# Revit family: Shower-Valve_Trim-KOHLER-MODULO-K-99960T_1
name_source: partatom
category: Plumbing Fixtures
revit_build: Autodesk Revit 2017 (Build: 20160225_1515(x64)
units: mm (PartAtom-declared; Revit-internal decimal feet)

## family parameters
Cut with Voids When Loaded = No
Host = Face
OmniClass Number = 23.31.25.00
Part Type = Normal
Room Calculation Point = No
Round Connector Dimension = Use Diameter
Shared = No

## types (5) — shared parameters
ADA Compliant = No
Assembly Code = D2010700
CW Connection = Yes
Cold Water Inlet = Cold Water Inlet
Date Modified = 10/09/2020
Default Elevation = 42"
Description = Smart formula-shaped in-wall bathtub shower spool and panel—classic type (Mema handle)
Drain Included = No
Flow Rate = 0 GPM
HW Connection = Yes
Handle Clearance = 2 3/4"
Height = 7 1/16"
Hot Water Inlet = Hot Water Inlet
Length = 4 1/8"
Manufacturer = KOHLER Co.
Master Format 2014 = 22 42 23
Master Format 2014 Name = Residential Showers
Material = Premium Metal construction
Panel Thickness = 0"
Pressure = 116.03 psi
Product Documentation Link = https://files.kohler.com.cn
Product Name = MODULO
Product Page URL = https://www.kohler.com.cn
Tempered Water Outlet 1 = Tempered Water Outlet 1
Tempered Water Outlet 2 = Tempered Water Outlet 2
URL = http://www.kohler.com.cn
Vent Connection = No
Waste Connection = No
Waste Water Outlet = Waste Water Outlet
WaterSense Certified = No
Width = 5 1/2"

## per-type parameters (varying)
| type | Finish | Model | Type |
| AF-Flange Gold | Kohler-Metal-AF-Flange_Gold | K-99960T-4V-AF | 1 |
| BN-Roman Silver | Kohler-Metal-BN-Roman_Silver | K-99960T-4V-BN | 2 |
| SN-Champagne Gold | Kohler-Metal-SN-Champagne_Gold | K-99960T-4V-SN | 3 |
| RGD-Rose Gold | Kohler-Metal-RGD-Rose_Gold | K-99960T-4V-RGD | 4 |
| CP-Polished Chrome | Kohler-Metal-CP-Polished_Chrome | K-99960T-4V-CP | 5 |

## geometry (parser evidence)
native form markers: Sweep x4
no freeform markers — native parametric forms only
